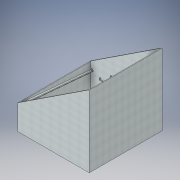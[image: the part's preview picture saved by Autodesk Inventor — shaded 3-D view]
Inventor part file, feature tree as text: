
AUTODESK INVENTOR PART (.ipt)
format: ipt  version: 2019.4 (Build 234330000, 330)  size: 309,248 bytes
history: native  units: mm
features: extrude x8, sketch x8, other x2, mirror x1
ambient origin geometry x8: Origin, YZ Plane, XZ Plane, XY Plane, X Axis, Y Axis, Z Axis, Center Point
bodies: Body1 (feature_tree)
feature tree (19):
  other  "Sólido1"
  extrude  "Extrusão1"  Depth=10.0mm TaperAngle=0.0deg
  extrude  "Extrusão2"  Depth=1000.0mm
  extrude  "Extrusão3"  Depth=350.0mm
  extrude  "Extrusão4"  Depth=10.0mm
  extrude  "Extrusão5"  Depth=10.0mm
  extrude  "Extrusão6"  Depth=6.0mm
  extrude  "Extrusão7"  Depth=10.0mm TaperAngle=0.0deg
  other  "Plano de trabalho1"
  mirror  "Espelhamento1"
  extrude  "Extrusão8"  Depth=10.0mm
  sketch  "Esboço1"  dims[d0=1000.0mm d1=0.0mm d2=10.0mm d3=0.0mm]
  sketch  "Esboço2"  dims[d4=10.0mm d5=0.0mm d6=1000.0mm]
  sketch  "Esboço3"  dims[d7=1000.0mm d8=350.0mm]
  sketch  "Esboço4"  dims[d10=10.0mm d11=14.835299mm]
  sketch  "Esboço5"  dims[d13=20.0mm d14=10.0mm]
  sketch  "Esboço6"  dims[d15=30.0mm d16=0.0mm d18=6.0mm]
  sketch  "Esboço7"  dims[d19=10.0mm d20=0.0mm d21=10.0mm d22=0.0mm]
  sketch  "Esboço8"  dims[d23=202.0mm d24=10.0mm d25=10.0mm d26=10.0mm d27=30.0mm d28=60.0mm d35=202.0mm d36=10.0mm d37=10.0mm d38=10.0mm d39=30.0mm d40=60.0mm d41=202.0mm d42=10.0mm d43=10.0mm d44=10.0mm d45=30.0mm d46=60.0mm d47=202.0mm d48=10.0mm d49=10.0mm d50=10.0mm d51=30.0mm d52=60.0mm d53=100.0mm d54=202.0mm d55=10.0mm d56=10.0mm d57=10.0mm d58=30.0mm d59=60.0mm d60=90.0mm d61=90.0mm d62=90.0mm d63=90.0mm d64=764.308998mm d65=140.0mm d66=10.0mm d67=0.0mm d68=31.05mm d69=20.0mm d70=10.0mm d71=0.0mm]
